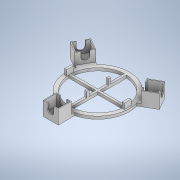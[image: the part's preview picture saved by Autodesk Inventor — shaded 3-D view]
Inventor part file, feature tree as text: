
AUTODESK INVENTOR PART (.ipt)
format: ipt  version: 2020 (Build 240168000, 168)  size: 265,216 bytes
history: native  units: mm
features: extrude x4, sketch x4, pattern_circular x1
ambient origin geometry x8: Origin, YZ Plane, XZ Plane, XY Plane, X Axis, Y Axis, Z Axis, Center Point
bodies: Solid1 (feature_tree)
feature tree (9):
  extrude  "Extrusion1"  Depth=100.0mm
  extrude  "Extrusion4"  Depth=4.0mm
  extrude  "Extrusion2"  Depth=100.0mm
  extrude  "Extrusion3"  Depth=60.0mm
  pattern_circular  "Circular Pattern1"  [2 undecoded]
  sketch  "Sketch1"  dims[d0=114.0mm d1=100.0mm]
  sketch  "Sketch2"  dims[d6=100.0mm d7=4.0mm]
  sketch  "Sketch4"  dims[d8=4.0mm d9=100.0mm]
  sketch  "Sketch5"  dims[d10=27.5mm d14=60.0mm d15=25.0mm d16=30.0mm d18=360.0deg d20=5.0mm d21=0.0mm d22=24.0mm d23=1.5mm d24=30.0mm d26=360.0deg d28=20.0mm d29=0.0mm d30=30.0mm d31=360.0deg d36=12.0mm d37=5.0mm d38=6.0mm d39=46.0mm d40=0.0mm d41=17.5mm d42=4.0mm d43=12.0mm d44=10.0mm d45=0.0mm]
note: 2 required parameter values undecoded (feature->parameter linkage not recoverable at this tier; creation-order binding heuristic only, values carry confidence <= 0.55)
